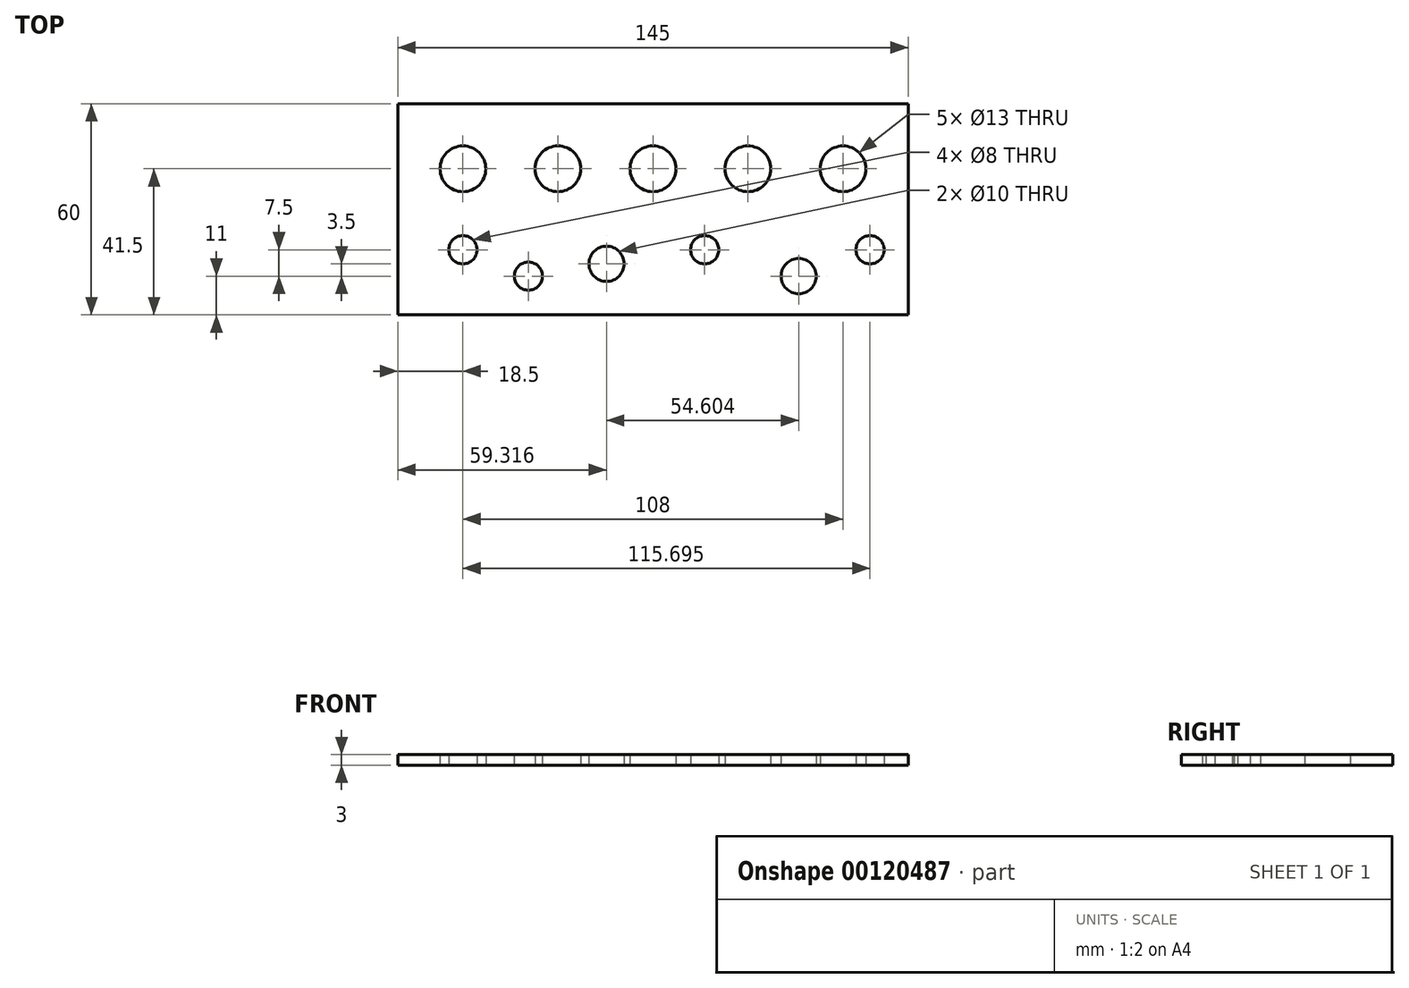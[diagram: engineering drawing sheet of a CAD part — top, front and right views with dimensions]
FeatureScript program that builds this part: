
annotation { "Feature Type Name" : "Feature", "Feature Type Description" : "" }
export const myFeature = defineFeature(function(context is Context, id is Id, definition is map)
    precondition{}
    {
        {
            var Q0;
            Q0=qCreatedBy(makeId("Top.planeOp"),FACE);
            var sketch = newSketch(context, id + "F0", { "sketchPlane" : qUnion([Q0])});
            skLineSegment(sketch, "E0.bottom", {"start": v(0, 0) * mm, "end": v(145, 0) * mm});
            skLineSegment(sketch, "E0.top", {"start": v(0, -60) * mm, "end": v(145, -60) * mm});
            skLineSegment(sketch, "E0.left", {"start": v(0, 0) * mm, "end": v(0, -60) * mm});
            skLineSegment(sketch, "E0.right", {"start": v(145, 0) * mm, "end": v(145, -60) * mm});
            skCircle(sketch, "E1", {"center": v(18.5, -18.5) * mm, "radius": 6.5 * mm});
            skCircle(sketch, "E2", {"center": v(126.5, -18.5) * mm, "radius": 6.5 * mm});
            skCircle(sketch, "E3", {"center": v(45.5, -18.5) * mm, "radius": 6.5 * mm});
            skCircle(sketch, "E4", {"center": v(72.5, -18.5) * mm, "radius": 6.5 * mm});
            skCircle(sketch, "E5", {"center": v(99.5, -18.5) * mm, "radius": 6.5 * mm});
            skCircle(sketch, "E6", {"center": v(18.5, -41.5) * mm, "radius": 4 * mm});
            skCircle(sketch, "E7", {"center": v(37.1, -49) * mm, "radius": 4 * mm});
            skCircle(sketch, "E8", {"center": v(59.32, -45.5) * mm, "radius": 5 * mm});
            skCircle(sketch, "E9", {"center": v(113.92, -49) * mm, "radius": 5 * mm});
            skCircle(sketch, "E10", {"center": v(87.2, -41.5) * mm, "radius": 4 * mm});
            skCircle(sketch, "E11", {"center": v(134.2, -41.5) * mm, "radius": 4 * mm});
            skSolve(sketch);
        }
        {
            var Q0;
            Q0=makeQuery(id+"F0.imprint","IMPRINT",FACE,{"disambiguationData":[TD([[makeQuery(id+"F0.imprint","IMPRINT",EDGE,{"derivedFrom":sQuery(id+"F0.wireOp",EDGE,"E0.bottom")}),-1.0]])]});
            extrude(context, id + "F1", {"entities" : qUnion([Q0]), "depth" : 3 * mm});
        }
    });
